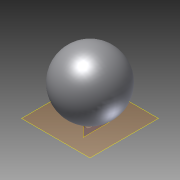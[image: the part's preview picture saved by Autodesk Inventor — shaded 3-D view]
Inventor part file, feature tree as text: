
AUTODESK INVENTOR PART (.ipt)
format: ipt  version: 2012 SP2 (Build 160219200, 219)  size: 128,000 bytes
history: native  units: in
note: dims shown in document units (in); Inventor stores cm internally (conversion verified against a paired STEP export)
features: sketch x3, plane x2, revolve x1, sweep x1
ambient origin geometry x8: Origin, YZ Plane, XZ Plane, XY Plane, X Axis, Y Axis, Z Axis, Center Point
bodies: Solid1 (feature_tree)
feature tree (7):
  revolve  "Revolution1"  [1 undecoded]
  plane  "Work Plane1"
  sketch  "Sketch2"  dims[d2=14.1755in d3=0.0in]
  plane  "Work Plane2"
  sweep  "Sweep1"
  sketch  "Sketch1"  dims[d0=180.0deg d1=0.7136in]
  sketch  "Sketch3"
note: 1 required parameter value undecoded (feature->parameter linkage not recoverable at this tier; creation-order binding heuristic only, values carry confidence <= 0.55)
